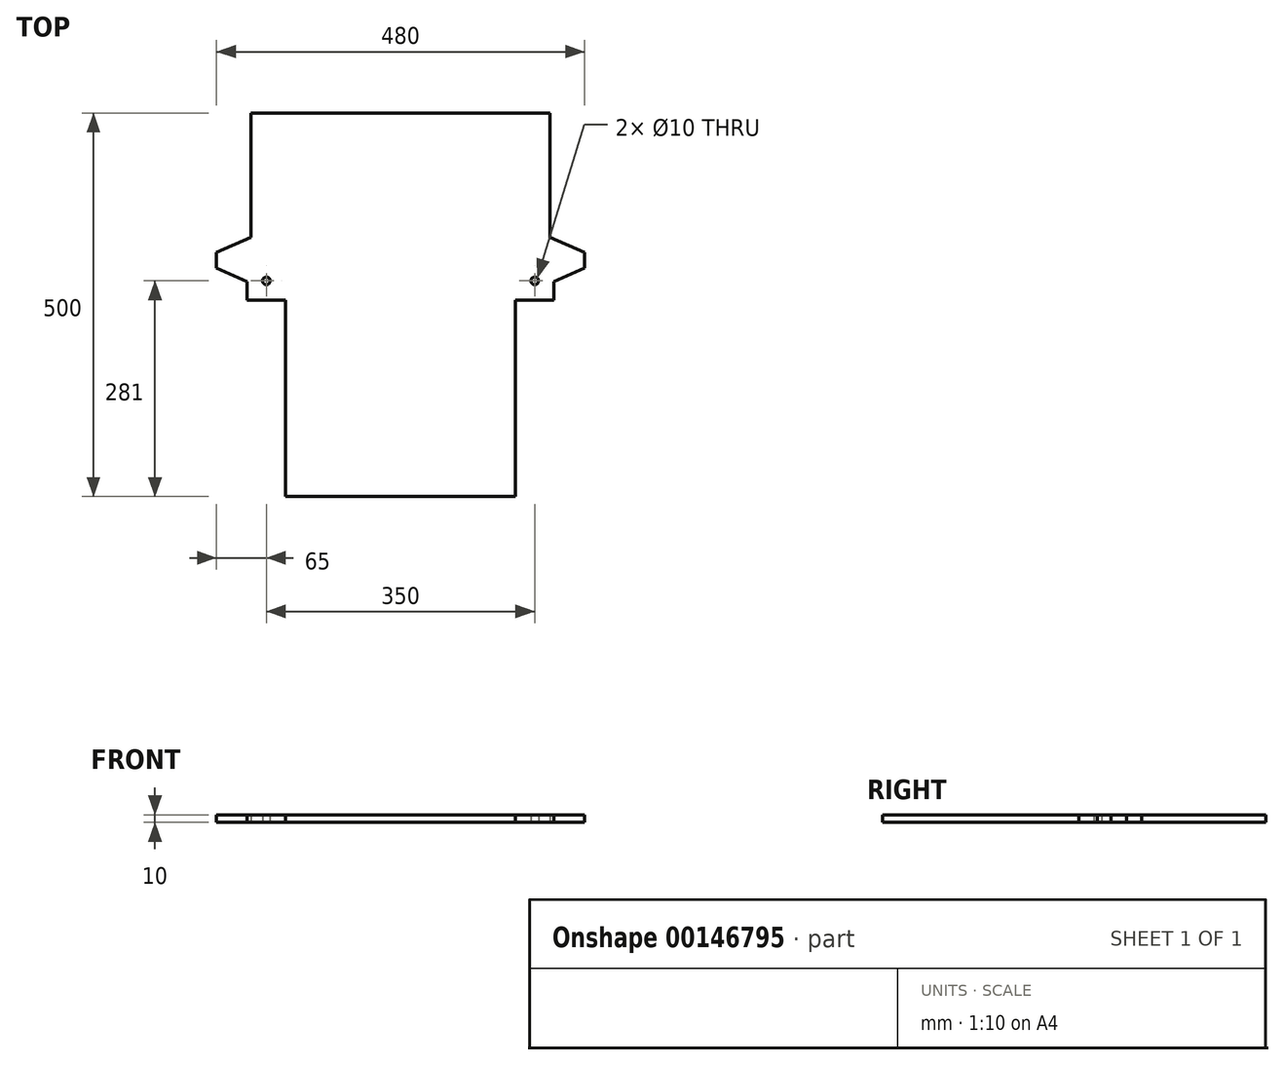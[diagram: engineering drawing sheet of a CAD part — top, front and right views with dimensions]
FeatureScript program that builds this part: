
annotation { "Feature Type Name" : "Feature", "Feature Type Description" : "" }
export const myFeature = defineFeature(function(context is Context, id is Id, definition is map)
    precondition{}
    {
        {
            var Q0;
            Q0=qCreatedBy(makeId("Top.planeOp"),FACE);
            var sketch = newSketch(context, id + "F0", { "sketchPlane" : qUnion([Q0])});
            skLineSegment(sketch, "E0", {"start": v(0, 305.95) * mm, "end": v(0, -346) * mm, "construction": true});
            skLineSegment(sketch, "E1", {"start": v(-175, 182) * mm, "end": v(-175, 0) * mm, "construction": true});
            skLineSegment(sketch, "E2", {"start": v(-230, 0) * mm, "end": v(-150, 0) * mm, "construction": true});
            skLineSegment(sketch, "E3", {"start": v(-240, 10) * mm, "end": v(-195, 30) * mm});
            skLineSegment(sketch, "E4", {"start": v(-195, 30) * mm, "end": v(-195, 192) * mm});
            skLineSegment(sketch, "E5", {"start": v(-195, 192) * mm, "end": v(0, 192) * mm});
            skLineSegment(sketch, "E6", {"start": v(-240, 10) * mm, "end": v(-240, -10) * mm});
            skLineSegment(sketch, "E7", {"start": v(-240, -10) * mm, "end": v(-200, -27.78) * mm});
            skLineSegment(sketch, "E8", {"start": v(-150, -52) * mm, "end": v(-150, -308) * mm});
            skLineSegment(sketch, "E9", {"start": v(-150, -308) * mm, "end": v(0, -308) * mm});
            skLineSegment(sketch, "E10", {"start": v(-195, 30) * mm, "end": v(-195, 0) * mm, "construction": true});
            skLineSegment(sketch, "E11", {"start": v(-195, 0) * mm, "end": v(-195, -30) * mm, "construction": true});
            skLineSegment(sketch, "E12", {"start": v(-200, 0) * mm, "end": v(-200, -52) * mm});
            skLineSegment(sketch, "E13", {"start": v(-200, -52) * mm, "end": v(-150, -52) * mm});
            skPoint(sketch, "E14.orphan", {"position": v(-150, -50) * mm});
            skLineSegment(sketch, "E15.MirrorCS", {"start": v(195, 30) * mm, "end": v(195, 0) * mm, "construction": true});
            skLineSegment(sketch, "E16.MirrorCS", {"start": v(240, 10) * mm, "end": v(240, -10) * mm});
            skLineSegment(sketch, "E17.MirrorCS", {"start": v(195, 0) * mm, "end": v(195, -30) * mm, "construction": true});
            skLineSegment(sketch, "E18.MirrorCS", {"start": v(200, 0) * mm, "end": v(200, -52) * mm});
            skLineSegment(sketch, "E19.MirrorCS", {"start": v(200, -52) * mm, "end": v(150, -52) * mm});
            skLineSegment(sketch, "E20.MirrorCS", {"start": v(230, 0) * mm, "end": v(150, 0) * mm, "construction": true});
            skLineSegment(sketch, "E21.MirrorCS", {"start": v(240, 10) * mm, "end": v(195, 30) * mm});
            skLineSegment(sketch, "E22.MirrorCS", {"start": v(240, -10) * mm, "end": v(200, -27.78) * mm});
            skLineSegment(sketch, "E23.MirrorCS", {"start": v(150, -52) * mm, "end": v(150, -308) * mm});
            skLineSegment(sketch, "E24.MirrorCS", {"start": v(195, 30) * mm, "end": v(195, 192) * mm});
            skPoint(sketch, "E25.MirrorP", {"position": v(150, -50) * mm});
            skLineSegment(sketch, "E26.MirrorCS", {"start": v(175, 182) * mm, "end": v(175, 0) * mm, "construction": true});
            skLineSegment(sketch, "E27.MirrorCS", {"start": v(195, 192) * mm, "end": v(0, 192) * mm});
            skLineSegment(sketch, "E28.MirrorCS", {"start": v(150, -308) * mm, "end": v(0, -308) * mm});
            skCircle(sketch, "E29", {"center": v(-175, -27) * mm, "radius": 5 * mm});
            skCircle(sketch, "E30.MirrorC", {"center": v(175, -27) * mm, "radius": 5 * mm});
            skSolve(sketch);
        }
        {
            var Q0;
            Q0 = qSketchRegion(id + "F0", true);
            extrude(context, id + "F1", {"entities" : qUnion([Q0]), "depth" : 10 * mm});
        }
    });
